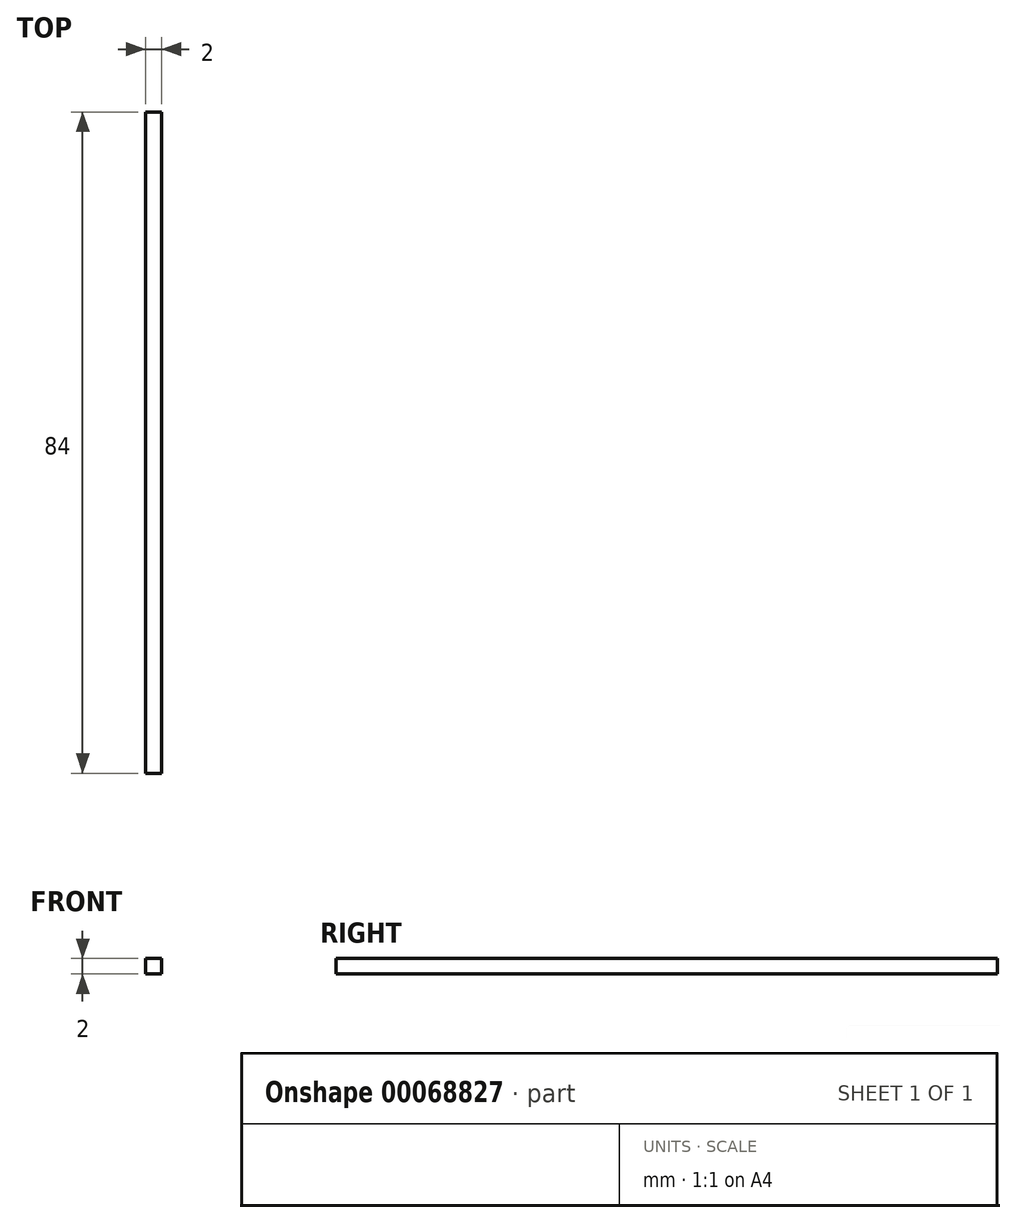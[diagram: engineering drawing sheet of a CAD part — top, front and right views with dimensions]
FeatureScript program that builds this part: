
annotation { "Feature Type Name" : "Feature", "Feature Type Description" : "" }
export const myFeature = defineFeature(function(context is Context, id is Id, definition is map)
    precondition{}
    {
        {
            var Q0;
            Q0=qCreatedBy(makeId("Top.planeOp"),FACE);
            var sketch = newSketch(context, id + "F0", { "sketchPlane" : qUnion([Q0])});
            skLineSegment(sketch, "E0.bottom", {"start": v(0, 0) * mm, "end": v(2, 0) * mm});
            skLineSegment(sketch, "E0.top", {"start": v(0, 84) * mm, "end": v(2, 84) * mm});
            skLineSegment(sketch, "E0.left", {"start": v(0, 0) * mm, "end": v(0, 84) * mm});
            skLineSegment(sketch, "E0.right", {"start": v(2, 0) * mm, "end": v(2, 84) * mm});
            skSolve(sketch);
        }
        {
            var Q0;
            Q0 = qSketchRegion(id + "F0", true);
            extrude(context, id + "F1", {"entities" : qUnion([Q0]), "depth" : 2 * mm});
        }
    });
